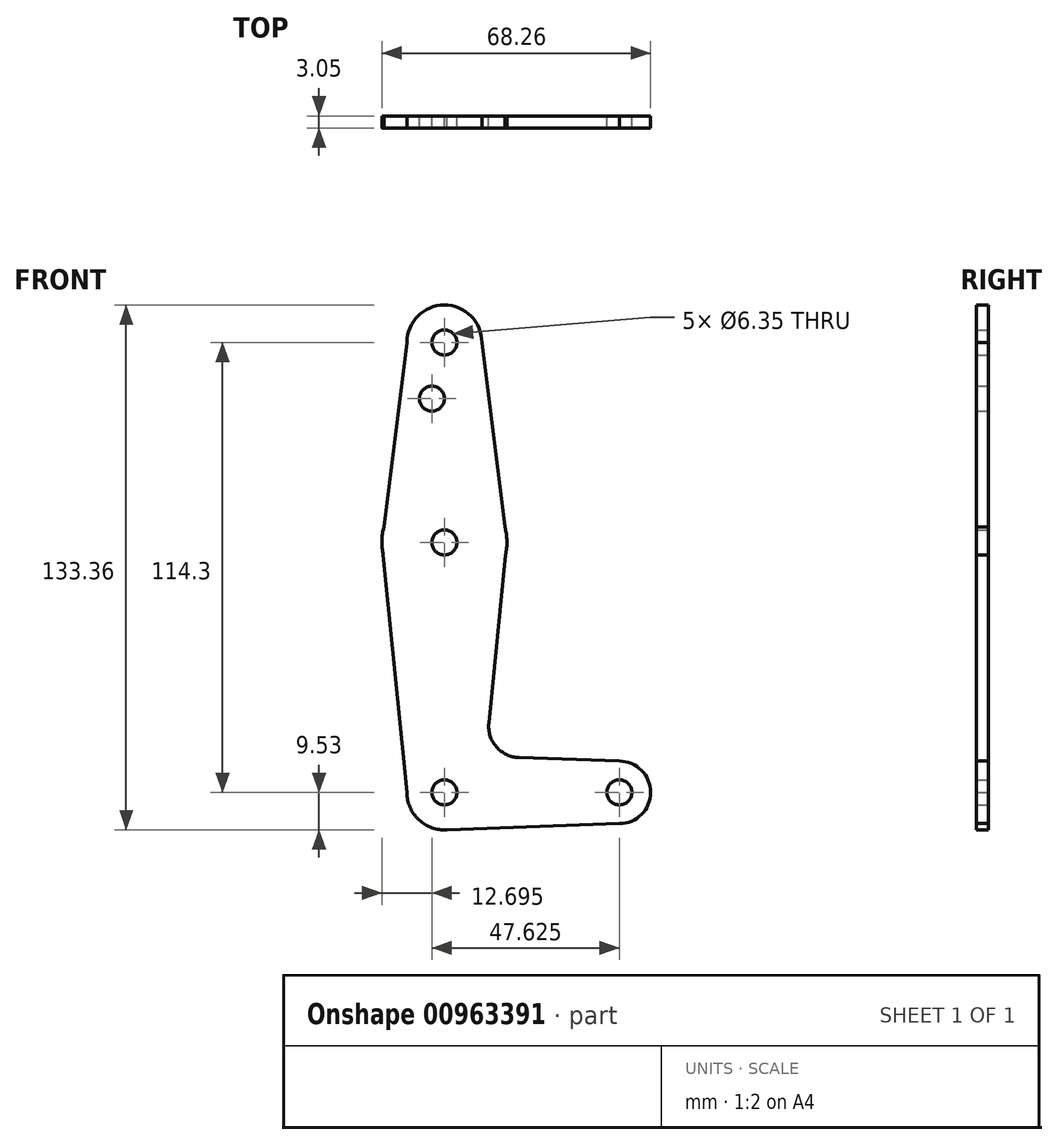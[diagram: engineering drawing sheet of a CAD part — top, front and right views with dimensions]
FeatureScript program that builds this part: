
annotation { "Feature Type Name" : "Feature", "Feature Type Description" : "" }
export const myFeature = defineFeature(function(context is Context, id is Id, definition is map)
    precondition{}
    {
        {
            var Q0;
            Q0=qCreatedBy(makeId("Front.planeOp"),FACE);
            var sketch = newSketch(context, id + "F0", { "sketchPlane" : qUnion([Q0])});
            skLineSegment(sketch, "E0", {"start": v(0, 0) * mm, "end": v(0, 114.3) * mm, "construction": true});
            skLineSegment(sketch, "E1", {"start": v(0, 0) * mm, "end": v(44.45, 0) * mm, "construction": true});
            skCircle(sketch, "E2", {"center": v(0, 114.3) * mm, "radius": 9.53 * mm});
            skCircle(sketch, "E3", {"center": v(0, 63.5) * mm, "radius": 15.88 * mm});
            skCircle(sketch, "E4", {"center": v(0, 0) * mm, "radius": 9.53 * mm});
            skCircle(sketch, "E5", {"center": v(44.45, 0) * mm, "radius": 7.94 * mm});
            skLineSegment(sketch, "E6", {"start": v(9.52, 114.3) * mm, "end": v(15.88, 63.5) * mm});
            skLineSegment(sketch, "E7", {"start": v(-9.52, 114.3) * mm, "end": v(-15.88, 63.5) * mm});
            skLineSegment(sketch, "E8", {"start": v(-15.88, 63.5) * mm, "end": v(-9.52, 0) * mm});
            skLineSegment(sketch, "E9", {"start": v(15.88, 63.5) * mm, "end": v(11.28, 17.59) * mm});
            skLineSegment(sketch, "E10", {"start": v(18.91, 8.85) * mm, "end": v(44.45, 7.94) * mm});
            skLineSegment(sketch, "E11", {"start": v(0, -9.52) * mm, "end": v(44.45, -7.94) * mm});
            skCircle(sketch, "E12", {"center": v(0, 114.3) * mm, "radius": 3.18 * mm});
            skCircle(sketch, "E13", {"center": v(0, 63.5) * mm, "radius": 3.18 * mm});
            skCircle(sketch, "E14", {"center": v(0, 0) * mm, "radius": 3.18 * mm});
            skCircle(sketch, "E15", {"center": v(44.45, 0) * mm, "radius": 3.18 * mm});
            skArc(sketch, "E16.filletArc", {"start": v(11.28, 17.59) * mm, "mid": v(13.2, 11.57) * mm, "end": v(18.91, 8.85) * mm});
            skCircle(sketch, "E17", {"center": v(-3.18, 100.03) * mm, "radius": 3.18 * mm});
            skSolve(sketch);
        }
        {
            var Q0;
            Q0 = qSketchRegion(id + "F0", true);
            extrude(context, id + "F1", {"entities" : qUnion([Q0]), "depth" : 3.05 * mm, "offsetDistance" : 25.4 * mm});
        }
    });
